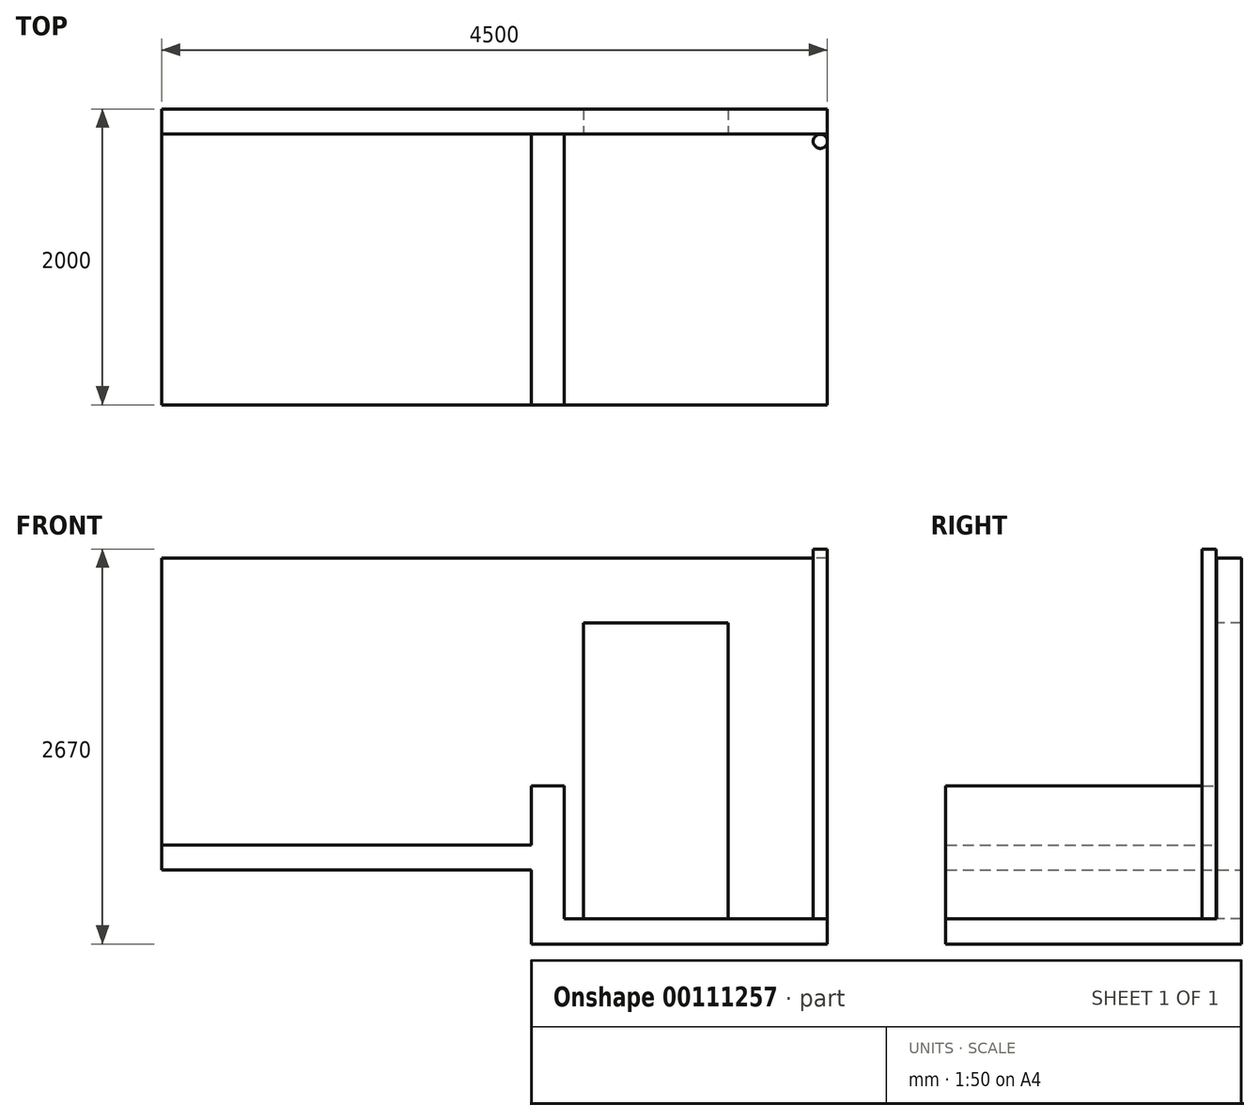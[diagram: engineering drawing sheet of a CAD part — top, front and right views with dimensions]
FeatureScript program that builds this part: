
annotation { "Feature Type Name" : "Feature", "Feature Type Description" : "" }
export const myFeature = defineFeature(function(context is Context, id is Id, definition is map)
    precondition{}
    {
        {
            var Q0;
            Q0=qCreatedBy(makeId("Front.planeOp"),FACE);
            var sketch = newSketch(context, id + "F0", { "sketchPlane" : qUnion([Q0])});
            skLineSegment(sketch, "E0", {"start": v(0, 0) * mm, "end": v(0, 400) * mm});
            skLineSegment(sketch, "E1", {"start": v(0, 400) * mm, "end": v(220, 400) * mm});
            skLineSegment(sketch, "E2", {"start": v(220, 400) * mm, "end": v(220, -500) * mm});
            skLineSegment(sketch, "E3", {"start": v(220, -500) * mm, "end": v(350, -500) * mm});
            skLineSegment(sketch, "E4", {"start": v(350, -500) * mm, "end": v(350, 1500) * mm});
            skLineSegment(sketch, "E5", {"start": v(350, 1500) * mm, "end": v(1330, 1500) * mm});
            skLineSegment(sketch, "E6", {"start": v(1330, 1500) * mm, "end": v(1330, -500) * mm});
            skLineSegment(sketch, "E7", {"start": v(1330, -500) * mm, "end": v(2000, -500) * mm});
            skLineSegment(sketch, "E8", {"start": v(2000, -500) * mm, "end": v(2000, 1940) * mm});
            skLineSegment(sketch, "E9", {"start": v(2000, 1940) * mm, "end": v(-2500, 1940) * mm});
            skLineSegment(sketch, "E10", {"start": v(-2500, 1940) * mm, "end": v(-2500, 0) * mm});
            skLineSegment(sketch, "E11", {"start": v(-2500, 0) * mm, "end": v(0, 0) * mm});
            skSolve(sketch);
        }
        {
            var Q0;
            Q0 = qSketchRegion(id + "F0", true);
            extrude(context, id + "F1", {"entities" : qUnion([Q0]), "oppositeDirection" : true, "depth" : 170 * mm});
        }
        {
            var Q0;
            Q0=makeQuery(id+"F1.opExtrude","CAP_FACE",FACE,{"disambiguationData":[OSD([sQuery(id+"F0.wireOp",EDGE,"E0"),sQuery(id+"F0.wireOp",EDGE,"E1"),sQuery(id+"F0.wireOp",EDGE,"E2"),sQuery(id+"F0.wireOp",EDGE,"E3"),sQuery(id+"F0.wireOp",EDGE,"E4"),sQuery(id+"F0.wireOp",EDGE,"E5"),sQuery(id+"F0.wireOp",EDGE,"E6"),sQuery(id+"F0.wireOp",EDGE,"E7"),sQuery(id+"F0.wireOp",EDGE,"E8"),sQuery(id+"F0.wireOp",EDGE,"E9"),sQuery(id+"F0.wireOp",EDGE,"E10"),sQuery(id+"F0.wireOp",EDGE,"E11")])],"isStart":false});
            var sketch = newSketch(context, id + "F2", { "sketchPlane" : qUnion([Q0])});
            skLineSegment(sketch, "E12", {"start": v(2500, 0) * mm, "end": v(0, 0) * mm});
            skLineSegment(sketch, "E13", {"start": v(0, 0) * mm, "end": v(0, 400) * mm});
            skLineSegment(sketch, "E14", {"start": v(0, 400) * mm, "end": v(-220, 400) * mm});
            skLineSegment(sketch, "E15", {"start": v(-220, 400) * mm, "end": v(-220, -500) * mm});
            skLineSegment(sketch, "E16", {"start": v(-220, -500) * mm, "end": v(-2000, -500) * mm});
            skLineSegment(sketch, "E17", {"start": v(-2000, -500) * mm, "end": v(-2000, -670) * mm});
            skLineSegment(sketch, "E18", {"start": v(-2000, -670) * mm, "end": v(0, -670) * mm});
            skLineSegment(sketch, "E19", {"start": v(0, -670) * mm, "end": v(0, -170) * mm});
            skLineSegment(sketch, "E20", {"start": v(0, -170) * mm, "end": v(2500, -170) * mm});
            skLineSegment(sketch, "E21", {"start": v(2500, -170) * mm, "end": v(2500, 0) * mm});
            skSolve(sketch);
        }
        {
            var Q0;
            Q0 = qSketchRegion(id + "F2", true);
            extrude(context, id + "F3", {"entities" : qUnion([Q0]), "operationType" : NewBodyOperationType.ADD, "oppositeDirection" : true, "depth" : 2000 * mm});
        }
        {
            var Q0;
            Q0=makeQuery(id+"F3.opExtrude","SWEPT_FACE",FACE,{"disambiguationData":[OSD([sQuery(id+"F2.wireOp",EDGE,"E16")])]});
            var sketch = newSketch(context, id + "F4", { "sketchPlane" : qUnion([Q0])});
            skCircle(sketch, "E22", {"center": v(1952, -49) * mm, "radius": 48 * mm});
            skSolve(sketch);
        }
        {
            var Q0;
            Q0 = qSketchRegion(id + "F4", true);
            extrude(context, id + "F5", {"entities" : qUnion([Q0]), "operationType" : NewBodyOperationType.ADD, "depth" : 2500 * mm});
        }
    });
